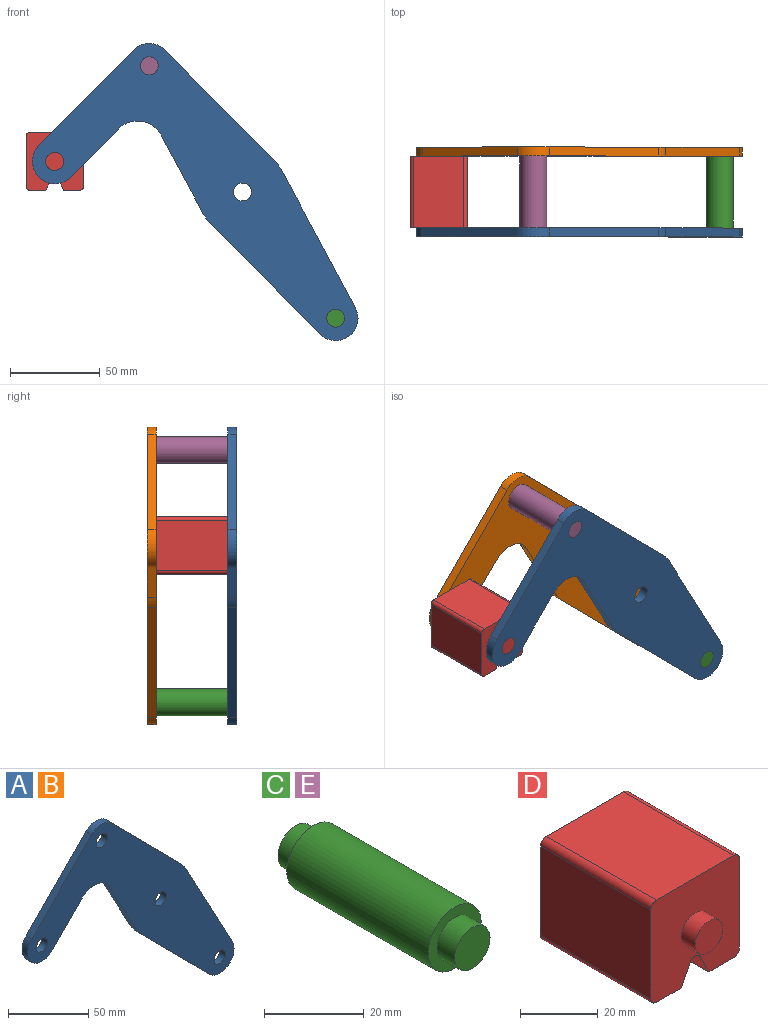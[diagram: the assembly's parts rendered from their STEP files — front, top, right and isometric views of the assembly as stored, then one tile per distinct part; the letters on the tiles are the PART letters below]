
ASSEMBLY  parts=5 mates=3
PART A: 18 faces, bbox 181.7x5x165.8 mm
  f0: plane 43.49x23.35mm, normal (-0.88,0,-0.47), area 246.8mm2, adj f1,f14,f16,f17
  f1: cylinder r=25mm len=5.75mm, axis (0,1,0), area 35.8mm2, adj f0,f2,f16,f17
  f2: plane 61.6x60.87mm, normal (-0.71,0,-0.7), area 433mm2, adj f1,f3,f16,f17
  f3: cylinder r=12.5mm len=21.39mm, axis (0,1,0), area 178.4mm2, adj f2,f4,f16,f17
  f4: plane 76.3x40.96mm, normal (0.88,0,0.47), area 433mm2, adj f3,f5,f16,f17
  f5: cylinder r=25mm len=5.75mm, axis (0,1,0), area 35.8mm2, adj f4,f6,f16,f17
  f6: plane 61.6x60.87mm, normal (0.71,0,0.7), area 433mm2, adj f5,f7,f16,f17
  f7: cylinder r=12.5mm len=17.78mm, axis (0,1,0), area 98.9mm2, adj f6,f8,f16,f17
  f8: plane 53.35x52.71mm, normal (-0.71,0,0.7), area 375mm2, adj f7,f9,f16,f17
  f9: cylinder r=12.5mm len=21.39mm, axis (0,1,0), area 196.3mm2, adj f8,f10,f16,f17
  f10: plane 26.86x26.54mm, normal (0.71,0,-0.7), area 188.8mm2, adj f9,f14,f16,f17
  f11: cylinder r=5mm len=10mm, axis (0,1,0), area 157.1mm2, adj f16,f17
  f12: cylinder r=5mm len=10mm, axis (0,1,0), area 157.1mm2, adj f16,f17
  f13: cylinder r=5mm len=10mm, axis (0,1,0), area 157.1mm2, adj f16,f17
  f14: cylinder r=15mm len=23.89mm, axis (0,1,0), area 140.2mm2, adj f0,f10,f16,f17
  f15: cylinder r=5mm len=10mm, axis (0,1,0), area 157.1mm2, adj f16,f17
  f16: plane 181.66x165.78mm, normal (0,-1,0), area 8710.1mm2, adj f0,f1,f2,f3,f4,f5,f6,f7
  f17: plane 181.66x165.78mm, normal (0,1,0), area 8710.1mm2, adj f0,f1,f2,f3,f4,f5,f6,f7
PART B: same geometry as A
PART C: 7 faces, bbox 15x50x15 mm
  f0: cylinder r=7.5mm len=40mm, axis (0,-1,0), area 1885mm2, adj f2,f5
  f1: cylinder r=5mm len=10mm, axis (0,1,0), area 157.1mm2, adj f2,f3
  f2: plane 15x15mm, normal (0,-1,0), area 98.2mm2, adj f0,f1
  f3: plane 10x10mm, normal (0,-1,0), area 78.5mm2, adj f1
  f4: cylinder r=5mm len=10mm, axis (0,-1,0), area 157.1mm2, adj f5,f6
  f5: plane 15x15mm, normal (0,1,0), area 98.2mm2, adj f0,f4
  f6: plane 10x10mm, normal (0,1,0), area 78.5mm2, adj f4
PART D: 18 faces, bbox 32.1x50x32.1 mm
  f0: plane 40x28.08mm, normal (1,0,0), area 1123.1mm2, adj f4,f10,f13,f14
  f1: plane 40x9.04mm, normal (0,0,-1), area 361.6mm2, adj f2,f4,f10,f14
  f2: plane 40x6.42mm, normal (-0.89,0,-0.45), area 287.2mm2, adj f1,f4,f10,f15
  f3: plane 40x6.42mm, normal (0.89,0,-0.45), area 287.2mm2, adj f4,f5,f10,f15
  f4: plane 32.08x32.08mm, normal (0,-1,0), area 900.6mm2, adj f0,f1,f2,f3,f5,f6,f7,f9
  f5: plane 40x9.04mm, normal (0,0,-1), area 361.6mm2, adj f3,f4,f10,f16
  f6: plane 40x28.08mm, normal (0,0,1), area 1123.1mm2, adj f4,f10,f13,f17
  f7: plane 40x28.08mm, normal (-1,0,0), area 1123.1mm2, adj f4,f10,f16,f17
  f8: plane 10x10mm, normal (0,-1,0), area 78.5mm2, adj f9
  f9: cylinder r=5mm len=10mm, axis (0,1,0), area 157.1mm2, adj f4,f8
  f10: plane 32.08x32.08mm, normal (0,1,0), area 900.6mm2, adj f0,f1,f2,f3,f5,f6,f7,f12
  f11: plane 10x10mm, normal (0,1,0), area 78.5mm2, adj f12
  f12: cylinder r=5mm len=10mm, axis (0,-1,0), area 157.1mm2, adj f10,f11
  f13: cylinder r=2mm len=40mm, axis (0,1,0), area 125.7mm2, adj f0,f4,f6,f10
  f14: cylinder r=2mm len=40mm, axis (0,-1,0), area 125.7mm2, adj f0,f1,f4,f10
  f15: cylinder r=2mm len=40mm, axis (0,1,0), area 177.1mm2, adj f2,f3,f4,f10
  f16: cylinder r=2mm len=40mm, axis (0,1,0), area 125.7mm2, adj f4,f5,f7,f10
  f17: cylinder r=2mm len=40mm, axis (0,-1,0), area 125.7mm2, adj f4,f6,f7,f10
PART E: same geometry as C
PLACE A t=(0,-20,0)mm fixed
PLACE B t=(0,25,0)mm
PLACE C t=(103.95,-20,-140.78)mm
PLACE D t=(0,-20,0)mm
PLACE E t=(0,-20,0)mm
MATE fastened C.f0 <-> A.f3  axis (0,-1,0) through (51.98,-20,-70.39)mm
MATE revolute D.f9 <-> A.f9  axis (0,-1,0) through (-104.69,-20,17.04)mm
MATE fastened B.f7 <-> E.f0  axis (0,-1,0) through (-51.98,20,70.39)mm
